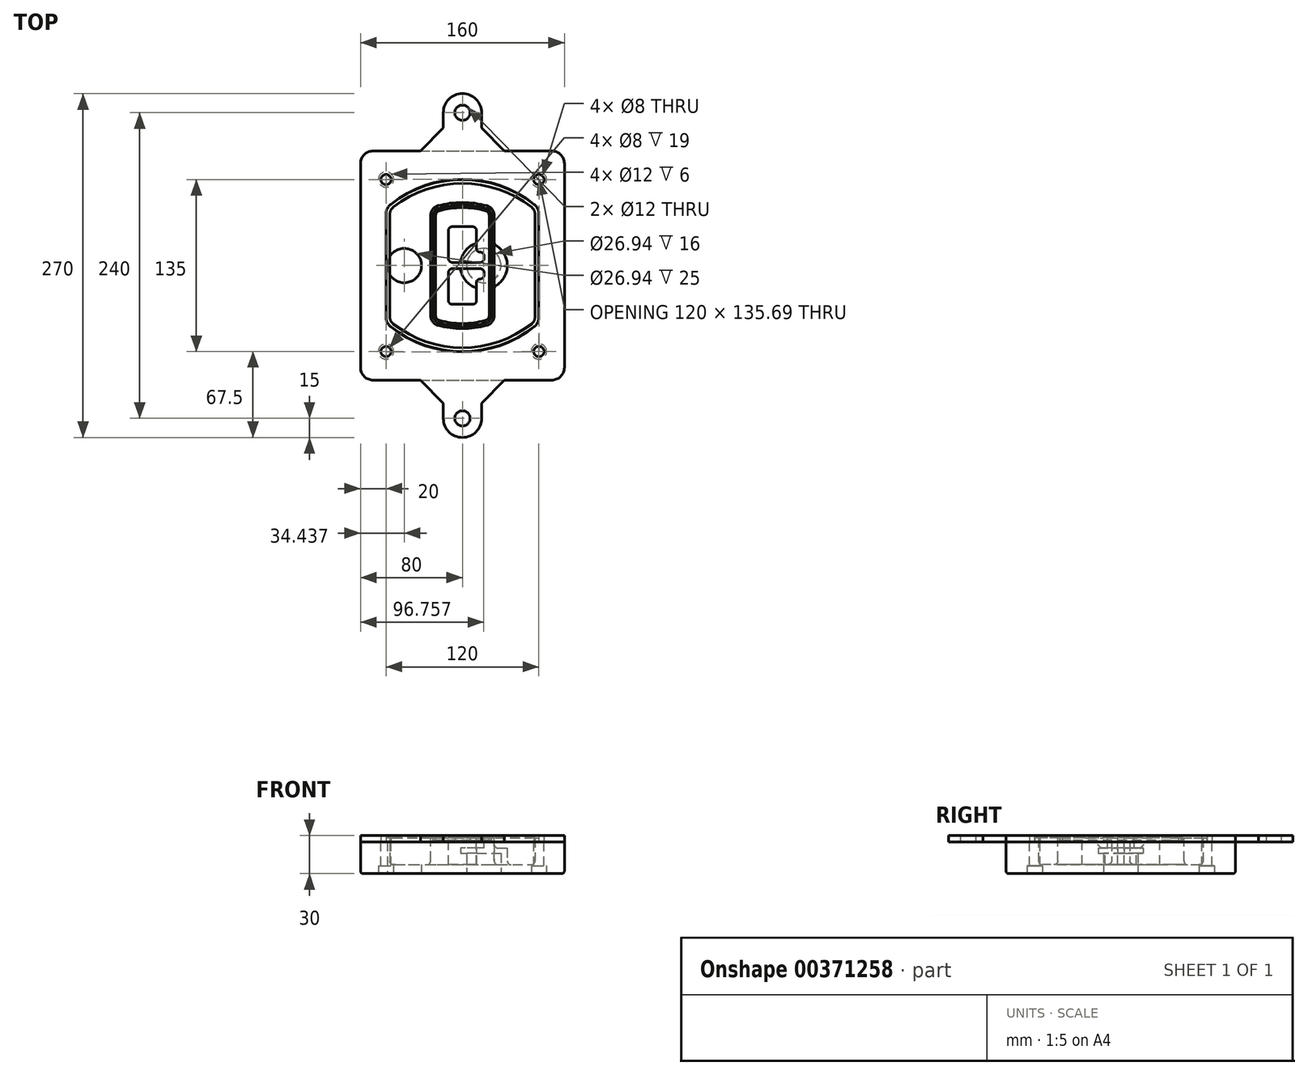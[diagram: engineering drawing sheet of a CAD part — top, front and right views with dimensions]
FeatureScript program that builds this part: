
annotation { "Feature Type Name" : "Feature", "Feature Type Description" : "" }
export const myFeature = defineFeature(function(context is Context, id is Id, definition is map)
    precondition{}
    {
        {
            var Q0;
            Q0=qCreatedBy(makeId("Top.planeOp"),FACE);
            var sketch = newSketch(context, id + "F0", { "sketchPlane" : qUnion([Q0])});
            skPoint(sketch, "E0.rect.middle", {"position": v(0, 0) * mm});
            skLineSegment(sketch, "E1.bottom", {"start": v(-70, -90) * mm, "end": v(70, -90) * mm});
            skLineSegment(sketch, "E1.top", {"start": v(-70, 90) * mm, "end": v(70, 90) * mm});
            skLineSegment(sketch, "E1.left", {"start": v(-80, -80) * mm, "end": v(-80, 80) * mm});
            skLineSegment(sketch, "E1.right", {"start": v(80, -80) * mm, "end": v(80, 80) * mm});
            skLineSegment(sketch, "E2", {"start": v(-80, 90) * mm, "end": v(80, -90) * mm, "construction": true});
            skLineSegment(sketch, "E3", {"start": v(80, 90) * mm, "end": v(-80, -90) * mm, "construction": true});
            skCircle(sketch, "E4", {"center": v(-60, 67.5) * mm, "radius": 4 * mm});
            skCircle(sketch, "E5", {"center": v(60, 67.5) * mm, "radius": 4 * mm});
            skCircle(sketch, "E6", {"center": v(60, -67.5) * mm, "radius": 4 * mm});
            skCircle(sketch, "E7", {"center": v(-60, -67.5) * mm, "radius": 4 * mm});
            skLineSegment(sketch, "E8", {"start": v(-60, 67.5) * mm, "end": v(60, 67.5) * mm, "construction": true});
            skLineSegment(sketch, "E9", {"start": v(60, 67.5) * mm, "end": v(60, -67.5) * mm, "construction": true});
            skLineSegment(sketch, "E10", {"start": v(60, -67.5) * mm, "end": v(-60, -67.5) * mm, "construction": true});
            skLineSegment(sketch, "E11", {"start": v(-60, -67.5) * mm, "end": v(-60, 67.5) * mm, "construction": true});
            skLineSegment(sketch, "E12", {"start": v(-60, 40.3) * mm, "end": v(-60, -40.3) * mm});
            skLineSegment(sketch, "E13", {"start": v(60, 40.3) * mm, "end": v(60, -40.3) * mm});
            skArc(sketch, "E14", {"start": v(56.15, 48.18) * mm, "mid": v(0, 67.5) * mm, "end": v(-56.15, 48.18) * mm});
            skArc(sketch, "E15", {"start": v(-56.15, -48.18) * mm, "mid": v(0, -67.5) * mm, "end": v(56.15, -48.18) * mm});
            skLineSegment(sketch, "E16", {"start": v(-60, 0) * mm, "end": v(60, 0) * mm, "construction": true});
            skPoint(sketch, "E17.visualSharp", {"position": v(-60, -45) * mm});
            skArc(sketch, "E17.filletArc", {"start": v(-60, -40.3) * mm, "mid": v(-58.99, -44.68) * mm, "end": v(-56.15, -48.18) * mm});
            skPoint(sketch, "E18.visualSharp", {"position": v(-60, 45) * mm});
            skArc(sketch, "E18.filletArc", {"start": v(-56.15, 48.18) * mm, "mid": v(-58.99, 44.68) * mm, "end": v(-60, 40.3) * mm});
            skPoint(sketch, "E19.visualSharp", {"position": v(60, 45) * mm});
            skArc(sketch, "E19.filletArc", {"start": v(60, 40.3) * mm, "mid": v(58.99, 44.68) * mm, "end": v(56.15, 48.18) * mm});
            skPoint(sketch, "E20.visualSharp", {"position": v(60, -45) * mm});
            skArc(sketch, "E20.filletArc", {"start": v(56.15, -48.18) * mm, "mid": v(58.99, -44.68) * mm, "end": v(60, -40.3) * mm});
            skPoint(sketch, "E21.visualSharp", {"position": v(-80, 90) * mm});
            skArc(sketch, "E21.filletArc", {"start": v(-70, 90) * mm, "mid": v(-77.07, 87.07) * mm, "end": v(-80, 80) * mm});
            skPoint(sketch, "E22.visualSharp", {"position": v(80, 90) * mm});
            skArc(sketch, "E22.filletArc", {"start": v(80, 80) * mm, "mid": v(77.07, 87.07) * mm, "end": v(70, 90) * mm});
            skPoint(sketch, "E23.visualSharp", {"position": v(80, -90) * mm});
            skArc(sketch, "E23.filletArc", {"start": v(70, -90) * mm, "mid": v(77.07, -87.07) * mm, "end": v(80, -80) * mm});
            skPoint(sketch, "E24.visualSharp", {"position": v(-80, -90) * mm});
            skArc(sketch, "E24.filletArc", {"start": v(-80, -80) * mm, "mid": v(-77.07, -87.07) * mm, "end": v(-70, -90) * mm});
            skArc(sketch, "E25.0", {"start": v(57, 40.3) * mm, "mid": v(56.3, 43.36) * mm, "end": v(54.3, 45.81) * mm});
            skLineSegment(sketch, "E25.1", {"start": v(57, 40.3) * mm, "end": v(57, -40.3) * mm});
            skArc(sketch, "E25.2", {"start": v(54.3, -45.81) * mm, "mid": v(56.3, -43.36) * mm, "end": v(57, -40.3) * mm});
            skArc(sketch, "E25.3", {"start": v(-54.3, -45.81) * mm, "mid": v(0, -64.5) * mm, "end": v(54.3, -45.81) * mm});
            skArc(sketch, "E25.4", {"start": v(-57, -40.3) * mm, "mid": v(-56.3, -43.36) * mm, "end": v(-54.3, -45.81) * mm});
            skArc(sketch, "E25.5", {"start": v(54.3, 45.81) * mm, "mid": v(0, 64.5) * mm, "end": v(-54.3, 45.81) * mm});
            skLineSegment(sketch, "E25.6", {"start": v(-57, 40.3) * mm, "end": v(-57, -40.3) * mm});
            skArc(sketch, "E25.7", {"start": v(-54.3, 45.81) * mm, "mid": v(-56.3, 43.36) * mm, "end": v(-57, 40.3) * mm});
            skArc(sketch, "E26.0", {"start": v(-58.62, 51.33) * mm, "mid": v(-62.58, 46.43) * mm, "end": v(-64, 40.3) * mm});
            skArc(sketch, "E26.1", {"start": v(58.62, 51.33) * mm, "mid": v(0, 71.5) * mm, "end": v(-58.62, 51.33) * mm});
            skArc(sketch, "E26.2", {"start": v(64, 40.3) * mm, "mid": v(62.58, 46.43) * mm, "end": v(58.62, 51.33) * mm});
            skLineSegment(sketch, "E26.3", {"start": v(64, 40.3) * mm, "end": v(64, -40.3) * mm});
            skArc(sketch, "E26.4", {"start": v(58.62, -51.33) * mm, "mid": v(62.58, -46.43) * mm, "end": v(64, -40.3) * mm});
            skLineSegment(sketch, "E26.5", {"start": v(-64, 40.3) * mm, "end": v(-64, -40.3) * mm});
            skArc(sketch, "E26.6", {"start": v(-58.62, -51.33) * mm, "mid": v(0, -71.5) * mm, "end": v(58.62, -51.33) * mm});
            skArc(sketch, "E26.7", {"start": v(-64, -40.3) * mm, "mid": v(-62.58, -46.43) * mm, "end": v(-58.62, -51.33) * mm});
            skSolve(sketch);
        }
        {
            var Q0;
            Q0=makeQuery(id+"F0.imprint","IMPRINT",FACE,{"disambiguationData":[TD([[makeQuery(id+"F0.imprint","IMPRINT",EDGE,{"derivedFrom":sQuery(id+"F0.wireOp",EDGE,"E1.bottom")}),1.0]])]});
            var Q1;
            Q1=makeQuery(id+"F0.imprint","IMPRINT",FACE,{"disambiguationData":[TD([[makeQuery(id+"F0.imprint","IMPRINT",EDGE,{"derivedFrom":sQuery(id+"F0.wireOp",EDGE,"E12")}),1.0]])]});
            var Q2;
            Q2=makeQuery(id+"F0.imprint","IMPRINT",FACE,{"disambiguationData":[TD([[makeQuery(id+"F0.imprint","IMPRINT",EDGE,{"derivedFrom":sQuery(id+"F0.wireOp",EDGE,"E25.0")}),1.0]])]});
            var Q3;
            Q3=makeQuery(id+"F0.imprint","IMPRINT",FACE,{"disambiguationData":[TD([[makeQuery(id+"F0.imprint","IMPRINT",EDGE,{"derivedFrom":sQuery(id+"F0.wireOp",EDGE,"E12")}),-1.0]])]});
            extrude(context, id + "F1", {"entities" : qUnion([Q0, Q1, Q2, Q3]), "oppositeDirection" : true, "depth" : 25 * mm});
        }
        {
            var Q0;
            Q0=makeQuery(id+"F0.imprint","IMPRINT",FACE,{"disambiguationData":[TD([[makeQuery(id+"F0.imprint","IMPRINT",EDGE,{"derivedFrom":sQuery(id+"F0.wireOp",EDGE,"E12")}),1.0]])]});
            extrude(context, id + "F2", {"entities" : qUnion([Q0]), "operationType" : NewBodyOperationType.ADD, "depth" : 3 * mm});
        }
        {
            var Q0;
            Q0=makeQuery(id+"F0.imprint","IMPRINT",FACE,{"disambiguationData":[TD([[makeQuery(id+"F0.imprint","IMPRINT",EDGE,{"derivedFrom":sQuery(id+"F0.wireOp",EDGE,"E25.0")}),1.0]])]});
            extrude(context, id + "F3", {"entities" : qUnion([Q0]), "operationType" : NewBodyOperationType.REMOVE, "oppositeDirection" : true, "depth" : 18 * mm});
        }
        {
            var Q0;
            Q0=makeQuery(id+"F2.opExtrude","CAP_FACE",FACE,{"disambiguationData":[OSD([sQuery(id+"F0.wireOp",EDGE,"E12"),sQuery(id+"F0.wireOp",EDGE,"E13"),sQuery(id+"F0.wireOp",EDGE,"E14"),sQuery(id+"F0.wireOp",EDGE,"E15"),sQuery(id+"F0.wireOp",EDGE,"E17.filletArc"),sQuery(id+"F0.wireOp",EDGE,"E18.filletArc"),sQuery(id+"F0.wireOp",EDGE,"E19.filletArc"),sQuery(id+"F0.wireOp",EDGE,"E20.filletArc"),sQuery(id+"F0.wireOp",EDGE,"E25.0"),sQuery(id+"F0.wireOp",EDGE,"E25.1"),sQuery(id+"F0.wireOp",EDGE,"E25.2"),sQuery(id+"F0.wireOp",EDGE,"E25.3"),sQuery(id+"F0.wireOp",EDGE,"E25.4"),sQuery(id+"F0.wireOp",EDGE,"E25.5"),sQuery(id+"F0.wireOp",EDGE,"E25.6"),sQuery(id+"F0.wireOp",EDGE,"E25.7")])],"isStart":false});
            var sketch = newSketch(context, id + "F4", { "sketchPlane" : qUnion([Q0])});
            skArc(sketch, "E27.0", {"start": v(-19.08, -46.97) * mm, "mid": v(0, -49.5) * mm, "end": v(19.08, -46.97) * mm});
            skArc(sketch, "E28.0", {"start": v(19.08, 46.97) * mm, "mid": v(0, 49.5) * mm, "end": v(-19.08, 46.97) * mm});
            skLineSegment(sketch, "E29", {"start": v(-25, 39.25) * mm, "end": v(-25, -39.25) * mm});
            skLineSegment(sketch, "E30", {"start": v(25, 39.25) * mm, "end": v(25, -39.25) * mm});
            skLineSegment(sketch, "E31", {"start": v(-25, 45.1) * mm, "end": v(25, 45.1) * mm, "construction": true});
            skLineSegment(sketch, "E32", {"start": v(-25, -45.1) * mm, "end": v(25, -45.1) * mm, "construction": true});
            skPoint(sketch, "E33.visualSharp", {"position": v(-25, 45.1) * mm});
            skArc(sketch, "E33.filletArc", {"start": v(-19.08, 46.97) * mm, "mid": v(-23.35, 44.11) * mm, "end": v(-25, 39.25) * mm});
            skPoint(sketch, "E34.visualSharp", {"position": v(25, 45.1) * mm});
            skArc(sketch, "E34.filletArc", {"start": v(25, 39.25) * mm, "mid": v(23.35, 44.11) * mm, "end": v(19.08, 46.97) * mm});
            skPoint(sketch, "E35.visualSharp", {"position": v(25, -45.1) * mm});
            skArc(sketch, "E35.filletArc", {"start": v(19.08, -46.97) * mm, "mid": v(23.35, -44.11) * mm, "end": v(25, -39.25) * mm});
            skPoint(sketch, "E36.visualSharp", {"position": v(-25, -45.1) * mm});
            skArc(sketch, "E36.filletArc", {"start": v(-25, -39.25) * mm, "mid": v(-23.35, -44.11) * mm, "end": v(-19.08, -46.97) * mm});
            skArc(sketch, "E37.0", {"start": v(54.3, 45.81) * mm, "mid": v(0, 64.5) * mm, "end": v(-54.3, 45.81) * mm});
            skArc(sketch, "E37.1", {"start": v(-54.3, 45.81) * mm, "mid": v(-56.3, 43.36) * mm, "end": v(-57, 40.3) * mm});
            skLineSegment(sketch, "E37.2", {"start": v(-57, 40.3) * mm, "end": v(-57, -40.3) * mm});
            skArc(sketch, "E37.3", {"start": v(-57, -40.3) * mm, "mid": v(-56.3, -43.36) * mm, "end": v(-54.3, -45.81) * mm});
            skArc(sketch, "E37.4", {"start": v(-54.3, -45.81) * mm, "mid": v(0, -64.5) * mm, "end": v(54.3, -45.81) * mm});
            skArc(sketch, "E37.5", {"start": v(54.3, -45.81) * mm, "mid": v(56.3, -43.36) * mm, "end": v(57, -40.3) * mm});
            skLineSegment(sketch, "E37.6", {"start": v(57, 40.3) * mm, "end": v(57, -40.3) * mm});
            skArc(sketch, "E37.7", {"start": v(57, 40.3) * mm, "mid": v(56.3, 43.36) * mm, "end": v(54.3, 45.81) * mm});
            skLineSegment(sketch, "E38.0", {"start": v(23, 39.25) * mm, "end": v(23, -39.25) * mm});
            skArc(sketch, "E38.1", {"start": v(18.56, -45.04) * mm, "mid": v(21.76, -42.9) * mm, "end": v(23, -39.25) * mm});
            skArc(sketch, "E38.2", {"start": v(-18.56, -45.04) * mm, "mid": v(0, -47.5) * mm, "end": v(18.56, -45.04) * mm});
            skArc(sketch, "E38.3", {"start": v(-23, -39.25) * mm, "mid": v(-21.76, -42.9) * mm, "end": v(-18.56, -45.04) * mm});
            skLineSegment(sketch, "E38.4", {"start": v(-23, 39.25) * mm, "end": v(-23, -39.25) * mm});
            skArc(sketch, "E38.5", {"start": v(23, 39.25) * mm, "mid": v(21.76, 42.9) * mm, "end": v(18.56, 45.04) * mm});
            skArc(sketch, "E38.6", {"start": v(-18.56, 45.04) * mm, "mid": v(-21.76, 42.9) * mm, "end": v(-23, 39.25) * mm});
            skArc(sketch, "E38.7", {"start": v(18.56, 45.04) * mm, "mid": v(0, 47.5) * mm, "end": v(-18.56, 45.04) * mm});
            skArc(sketch, "E39.0", {"start": v(21, 39.25) * mm, "mid": v(20.18, 41.68) * mm, "end": v(18.04, 43.1) * mm});
            skLineSegment(sketch, "E39.1", {"start": v(21, 39.25) * mm, "end": v(21, -39.25) * mm});
            skArc(sketch, "E39.2", {"start": v(18.04, -43.1) * mm, "mid": v(20.18, -41.68) * mm, "end": v(21, -39.25) * mm});
            skArc(sketch, "E39.3", {"start": v(-18.04, -43.1) * mm, "mid": v(0, -45.5) * mm, "end": v(18.04, -43.1) * mm});
            skArc(sketch, "E39.4", {"start": v(-21, -39.25) * mm, "mid": v(-20.18, -41.68) * mm, "end": v(-18.04, -43.1) * mm});
            skArc(sketch, "E39.5", {"start": v(18.04, 43.1) * mm, "mid": v(0, 45.5) * mm, "end": v(-18.04, 43.1) * mm});
            skLineSegment(sketch, "E39.6", {"start": v(-21, 39.25) * mm, "end": v(-21, -39.25) * mm});
            skArc(sketch, "E39.7", {"start": v(-18.04, 43.1) * mm, "mid": v(-20.18, 41.68) * mm, "end": v(-21, 39.25) * mm});
            skLineSegment(sketch, "E40", {"start": v(-25, 0) * mm, "end": v(25, 0) * mm, "construction": true});
            skLineSegment(sketch, "E41", {"start": v(-11, 5.5) * mm, "end": v(-11, 27.5) * mm});
            skLineSegment(sketch, "E42", {"start": v(-8, 30.5) * mm, "end": v(8, 30.5) * mm});
            skLineSegment(sketch, "E43", {"start": v(11, 27.5) * mm, "end": v(11, 13.5) * mm});
            skLineSegment(sketch, "E44", {"start": v(14, 10.5) * mm, "end": v(14, 10.5) * mm});
            skLineSegment(sketch, "E45", {"start": v(17, 7.5) * mm, "end": v(17, 5.5) * mm});
            skLineSegment(sketch, "E46", {"start": v(14, 2.5) * mm, "end": v(-8, 2.5) * mm});
            skPoint(sketch, "E47.visualSharp", {"position": v(-11, 30.5) * mm});
            skArc(sketch, "E47.filletArc", {"start": v(-8, 30.5) * mm, "mid": v(-10.12, 29.62) * mm, "end": v(-11, 27.5) * mm});
            skPoint(sketch, "E48.visualSharp", {"position": v(11, 30.5) * mm});
            skArc(sketch, "E48.filletArc", {"start": v(11, 27.5) * mm, "mid": v(10.12, 29.62) * mm, "end": v(8, 30.5) * mm});
            skPoint(sketch, "E49.visualSharp", {"position": v(11, 10.5) * mm});
            skArc(sketch, "E49.filletArc", {"start": v(11, 13.5) * mm, "mid": v(11.88, 11.38) * mm, "end": v(14, 10.5) * mm});
            skPoint(sketch, "E50.visualSharp", {"position": v(17, 10.5) * mm});
            skArc(sketch, "E50.filletArc", {"start": v(17, 7.5) * mm, "mid": v(16.12, 9.62) * mm, "end": v(14, 10.5) * mm});
            skPoint(sketch, "E51.visualSharp", {"position": v(17, 2.5) * mm});
            skArc(sketch, "E51.filletArc", {"start": v(14, 2.5) * mm, "mid": v(16.12, 3.38) * mm, "end": v(17, 5.5) * mm});
            skPoint(sketch, "E52.visualSharp", {"position": v(-11, 2.5) * mm});
            skArc(sketch, "E52.filletArc", {"start": v(-11, 5.5) * mm, "mid": v(-10.12, 3.38) * mm, "end": v(-8, 2.5) * mm});
            skLineSegment(sketch, "E53.0.MirrorCS", {"start": v(14, -2.5) * mm, "end": v(-8, -2.5) * mm});
            skArc(sketch, "E54.0.MirrorCS", {"start": v(-11, -5.5) * mm, "mid": v(-10.12, -3.38) * mm, "end": v(-8, -2.5) * mm});
            skLineSegment(sketch, "E55.0.MirrorCS", {"start": v(-11, -5.5) * mm, "end": v(-11, -27.5) * mm});
            skArc(sketch, "E56.0.MirrorCS", {"start": v(-8, -30.5) * mm, "mid": v(-10.12, -29.62) * mm, "end": v(-11, -27.5) * mm});
            skLineSegment(sketch, "E57.0.MirrorCS", {"start": v(-8, -30.5) * mm, "end": v(8, -30.5) * mm});
            skArc(sketch, "E58.0.MirrorCS", {"start": v(11, -27.5) * mm, "mid": v(10.12, -29.62) * mm, "end": v(8, -30.5) * mm});
            skLineSegment(sketch, "E59.0.MirrorCS", {"start": v(11, -27.5) * mm, "end": v(11, -13.5) * mm});
            skArc(sketch, "E60.0.MirrorCS", {"start": v(11, -13.5) * mm, "mid": v(11.88, -11.38) * mm, "end": v(14, -10.5) * mm});
            skArc(sketch, "E61.0.MirrorCS", {"start": v(17, -7.5) * mm, "mid": v(16.12, -9.62) * mm, "end": v(14, -10.5) * mm});
            skLineSegment(sketch, "E62.0.MirrorCS", {"start": v(17, -7.5) * mm, "end": v(17, -5.5) * mm});
            skArc(sketch, "E63.0.MirrorCS", {"start": v(14, -2.5) * mm, "mid": v(16.12, -3.38) * mm, "end": v(17, -5.5) * mm});
            skSolve(sketch);
        }
        {
            var Q0;
            Q0=makeQuery(id+"F4.imprint","IMPRINT",FACE,{"disambiguationData":[TD([[makeQuery(id+"F4.imprint","IMPRINT",EDGE,{"derivedFrom":sQuery(id+"F4.wireOp",EDGE,"E27.0")}),1.0]])]});
            var Q1;
            Q1=makeQuery(id+"F4.imprint","IMPRINT",FACE,{"disambiguationData":[TD([[makeQuery(id+"F4.imprint","IMPRINT",EDGE,{"derivedFrom":sQuery(id+"F4.wireOp",EDGE,"E38.0")}),-1.0]])]});
            var Q2;
            Q2=makeQuery(id+"F4.imprint","IMPRINT",FACE,{"disambiguationData":[TD([[makeQuery(id+"F4.imprint","IMPRINT",EDGE,{"derivedFrom":sQuery(id+"F4.wireOp",EDGE,"E39.0")}),1.0]])]});
            extrude(context, id + "F5", {"entities" : qUnion([Q0, Q1, Q2]), "operationType" : NewBodyOperationType.ADD, "endBound" : BoundingType.UP_TO_NEXT, "oppositeDirection" : true, "depth" : 25 * mm});
        }
        {
            var Q0;
            Q0=makeQuery(id+"F4.imprint","IMPRINT",FACE,{"disambiguationData":[TD([[makeQuery(id+"F4.imprint","IMPRINT",EDGE,{"derivedFrom":sQuery(id+"F4.wireOp",EDGE,"E38.0")}),-1.0]])]});
            extrude(context, id + "F6", {"entities" : qUnion([Q0]), "operationType" : NewBodyOperationType.REMOVE, "oppositeDirection" : true, "depth" : 2 * mm});
        }
        {
            var Q0;
            Q0=makeQuery(id+"F1.opExtrude","CAP_FACE",FACE,{"disambiguationData":[OSD([sQuery(id+"F0.wireOp",EDGE,"E1.bottom"),sQuery(id+"F0.wireOp",EDGE,"E1.top"),sQuery(id+"F0.wireOp",EDGE,"E1.left"),sQuery(id+"F0.wireOp",EDGE,"E1.right"),sQuery(id+"F0.wireOp",EDGE,"E4"),sQuery(id+"F0.wireOp",EDGE,"E5"),sQuery(id+"F0.wireOp",EDGE,"E6"),sQuery(id+"F0.wireOp",EDGE,"E7"),sQuery(id+"F0.wireOp",EDGE,"E21.filletArc"),sQuery(id+"F0.wireOp",EDGE,"E22.filletArc"),sQuery(id+"F0.wireOp",EDGE,"E23.filletArc"),sQuery(id+"F0.wireOp",EDGE,"E24.filletArc")])],"isStart":false});
            var sketch = newSketch(context, id + "F7", { "sketchPlane" : qUnion([Q0])});
            skCircle(sketch, "E64", {"center": v(16.76, 0) * mm, "radius": 13.47 * mm});
            skCircle(sketch, "E65", {"center": v(-45.56, 0) * mm, "radius": 13.47 * mm});
            skLineSegment(sketch, "E66", {"start": v(80, 0) * mm, "end": v(-80, 0) * mm});
            skCircle(sketch, "E67", {"center": v(16.76, 0) * mm, "radius": 18.47 * mm});
            skCircle(sketch, "E68", {"center": v(60, -67.5) * mm, "radius": 6 * mm});
            skCircle(sketch, "E69", {"center": v(-60, -67.5) * mm, "radius": 6 * mm});
            skCircle(sketch, "E70", {"center": v(-60, 67.5) * mm, "radius": 6 * mm});
            skCircle(sketch, "E71", {"center": v(60, 67.5) * mm, "radius": 6 * mm});
            skSolve(sketch);
        }
        {
            var Q0;
            {var subQ1=sQuery(id+"F7.wireOp",EDGE,"E66");var subQ4=sQuery(id+"F7.wireOp",EDGE,"E64");var subQ6=makeQuery(id+"F7.imprint","INTERSECT",VERTEX,{"disambiguationData":[OD(0.0)],"derivedFrom":[subQ4,subQ1]});Q0=makeQuery(id+"F7.imprint","IMPRINT",FACE,{"disambiguationData":[TD([[makeQuery(id+"F7.imprint","IMPRINT",EDGE,{"disambiguationData":[TD([[subQ6,-1.0]])],"derivedFrom":subQ4}),-1.0]])]});}
            var Q1;
            {var subQ0=sQuery(id+"F7.wireOp",EDGE,"E66");var subQ1=sQuery(id+"F7.wireOp",EDGE,"E64");var subQ3=makeQuery(id+"F7.imprint","INTERSECT",VERTEX,{"disambiguationData":[OD(0.0)],"derivedFrom":[subQ1,subQ0]});Q1=makeQuery(id+"F7.imprint","IMPRINT",FACE,{"disambiguationData":[TD([[makeQuery(id+"F7.imprint","IMPRINT",EDGE,{"disambiguationData":[TD([[subQ3,-1.0]])],"derivedFrom":subQ1}),1.0]])]});}
            var Q2;
            {var subQ0=sQuery(id+"F7.wireOp",EDGE,"E66");var subQ1=sQuery(id+"F7.wireOp",EDGE,"E64");var subQ3=makeQuery(id+"F7.imprint","INTERSECT",VERTEX,{"disambiguationData":[OD(0.0)],"derivedFrom":[subQ1,subQ0]});Q2=makeQuery(id+"F7.imprint","IMPRINT",FACE,{"disambiguationData":[TD([[makeQuery(id+"F7.imprint","IMPRINT",EDGE,{"disambiguationData":[TD([[subQ3,1.0]])],"derivedFrom":subQ1}),1.0]])]});}
            var Q3;
            {var subQ1=sQuery(id+"F7.wireOp",EDGE,"E66");var subQ4=sQuery(id+"F7.wireOp",EDGE,"E64");var subQ6=makeQuery(id+"F7.imprint","INTERSECT",VERTEX,{"disambiguationData":[OD(0.0)],"derivedFrom":[subQ4,subQ1]});Q3=makeQuery(id+"F7.imprint","IMPRINT",FACE,{"disambiguationData":[TD([[makeQuery(id+"F7.imprint","IMPRINT",EDGE,{"disambiguationData":[TD([[subQ6,1.0]])],"derivedFrom":subQ4}),-1.0]])]});}
            extrude(context, id + "F8", {"entities" : qUnion([Q0, Q1, Q2, Q3]), "operationType" : NewBodyOperationType.ADD, "oppositeDirection" : true, "depth" : 20 * mm});
        }
        {
            var Q0;
            {var subQ0=sQuery(id+"F7.wireOp",EDGE,"E66");var subQ1=sQuery(id+"F7.wireOp",EDGE,"E64");var subQ3=makeQuery(id+"F7.imprint","INTERSECT",VERTEX,{"disambiguationData":[OD(0.0)],"derivedFrom":[subQ1,subQ0]});Q0=makeQuery(id+"F7.imprint","IMPRINT",FACE,{"disambiguationData":[TD([[makeQuery(id+"F7.imprint","IMPRINT",EDGE,{"disambiguationData":[TD([[subQ3,-1.0]])],"derivedFrom":subQ1}),1.0]])]});}
            var Q1;
            {var subQ0=sQuery(id+"F7.wireOp",EDGE,"E66");var subQ1=sQuery(id+"F7.wireOp",EDGE,"E64");var subQ3=makeQuery(id+"F7.imprint","INTERSECT",VERTEX,{"disambiguationData":[OD(0.0)],"derivedFrom":[subQ1,subQ0]});Q1=makeQuery(id+"F7.imprint","IMPRINT",FACE,{"disambiguationData":[TD([[makeQuery(id+"F7.imprint","IMPRINT",EDGE,{"disambiguationData":[TD([[subQ3,1.0]])],"derivedFrom":subQ1}),1.0]])]});}
            extrude(context, id + "F9", {"entities" : qUnion([Q0, Q1]), "operationType" : NewBodyOperationType.REMOVE, "oppositeDirection" : true, "depth" : 16 * mm});
        }
        {
            var Q0;
            {var subQ0=sQuery(id+"F7.wireOp",EDGE,"E66");var subQ1=sQuery(id+"F7.wireOp",EDGE,"E65");var subQ3=makeQuery(id+"F7.imprint","INTERSECT",VERTEX,{"disambiguationData":[OD(0.0)],"derivedFrom":[subQ1,subQ0]});Q0=makeQuery(id+"F7.imprint","IMPRINT",FACE,{"disambiguationData":[TD([[makeQuery(id+"F7.imprint","IMPRINT",EDGE,{"disambiguationData":[TD([[subQ3,-1.0]])],"derivedFrom":subQ1}),1.0]])]});}
            var Q1;
            {var subQ0=sQuery(id+"F7.wireOp",EDGE,"E66");var subQ1=sQuery(id+"F7.wireOp",EDGE,"E65");var subQ3=makeQuery(id+"F7.imprint","INTERSECT",VERTEX,{"disambiguationData":[OD(0.0)],"derivedFrom":[subQ1,subQ0]});Q1=makeQuery(id+"F7.imprint","IMPRINT",FACE,{"disambiguationData":[TD([[makeQuery(id+"F7.imprint","IMPRINT",EDGE,{"disambiguationData":[TD([[subQ3,1.0]])],"derivedFrom":subQ1}),1.0]])]});}
            extrude(context, id + "F10", {"entities" : qUnion([Q0, Q1]), "operationType" : NewBodyOperationType.REMOVE, "oppositeDirection" : true, "depth" : 25 * mm});
        }
        {
            var Q0;
            Q0=makeQuery(id+"F7.imprint","IMPRINT",FACE,{"disambiguationData":[TD([[makeQuery(id+"F7.imprint","IMPRINT",EDGE,{"derivedFrom":sQuery(id+"F7.wireOp",EDGE,"E68")}),1.0]])]});
            var Q1;
            Q1=makeQuery(id+"F7.imprint","IMPRINT",FACE,{"disambiguationData":[TD([[makeQuery(id+"F7.imprint","IMPRINT",EDGE,{"derivedFrom":makeQuery(id+"F1.opExtrude","CAP_EDGE",EDGE,{"disambiguationData":[OSD([sQuery(id+"F0.wireOp",EDGE,"E5")])],"isStart":false})}),-1.0]])]});
            var Q2;
            Q2=makeQuery(id+"F7.imprint","IMPRINT",FACE,{"disambiguationData":[TD([[makeQuery(id+"F7.imprint","IMPRINT",EDGE,{"derivedFrom":sQuery(id+"F7.wireOp",EDGE,"E69")}),1.0]])]});
            var Q3;
            Q3=makeQuery(id+"F7.imprint","IMPRINT",FACE,{"disambiguationData":[TD([[makeQuery(id+"F7.imprint","IMPRINT",EDGE,{"derivedFrom":makeQuery(id+"F1.opExtrude","CAP_EDGE",EDGE,{"disambiguationData":[OSD([sQuery(id+"F0.wireOp",EDGE,"E4")])],"isStart":false})}),-1.0]])]});
            var Q4;
            Q4=makeQuery(id+"F7.imprint","IMPRINT",FACE,{"disambiguationData":[TD([[makeQuery(id+"F7.imprint","IMPRINT",EDGE,{"derivedFrom":sQuery(id+"F7.wireOp",EDGE,"E70")}),1.0]])]});
            var Q5;
            Q5=makeQuery(id+"F7.imprint","IMPRINT",FACE,{"disambiguationData":[TD([[makeQuery(id+"F7.imprint","IMPRINT",EDGE,{"derivedFrom":makeQuery(id+"F1.opExtrude","CAP_EDGE",EDGE,{"disambiguationData":[OSD([sQuery(id+"F0.wireOp",EDGE,"E7")])],"isStart":false})}),-1.0]])]});
            var Q6;
            Q6=makeQuery(id+"F7.imprint","IMPRINT",FACE,{"disambiguationData":[TD([[makeQuery(id+"F7.imprint","IMPRINT",EDGE,{"derivedFrom":sQuery(id+"F7.wireOp",EDGE,"E71")}),1.0]])]});
            var Q7;
            Q7=makeQuery(id+"F7.imprint","IMPRINT",FACE,{"disambiguationData":[TD([[makeQuery(id+"F7.imprint","IMPRINT",EDGE,{"derivedFrom":makeQuery(id+"F1.opExtrude","CAP_EDGE",EDGE,{"disambiguationData":[OSD([sQuery(id+"F0.wireOp",EDGE,"E6")])],"isStart":false})}),-1.0]])]});
            extrude(context, id + "F11", {"entities" : qUnion([Q0, Q1, Q2, Q3, Q4, Q5, Q6, Q7]), "operationType" : NewBodyOperationType.REMOVE, "oppositeDirection" : true, "depth" : 6 * mm});
        }
        {
            var Q0;
            Q0=makeQuery(id+"F9.boolean.opBoolean","COPY",FACE,{"derivedFrom":makeQuery(id+"F9.opExtrude","CAP_FACE",FACE,{"disambiguationData":[OSD([sQuery(id+"F7.wireOp",EDGE,"E64")])],"isStart":false})});
            var sketch = newSketch(context, id + "F12", { "sketchPlane" : qUnion([Q0])});
            skArc(sketch, "E72.0", {"start": v(11, 17.55) * mm, "mid": v(2.57, 11.82) * mm, "end": v(-1.54, 2.5) * mm});
            skArc(sketch, "E72.1", {"start": v(-1.54, -2.5) * mm, "mid": v(2.57, -11.82) * mm, "end": v(11, -17.55) * mm});
            skLineSegment(sketch, "E73", {"start": v(-1.54, -2.5) * mm, "end": v(14, -2.5) * mm});
            skLineSegment(sketch, "E74.0", {"start": v(14, 2.5) * mm, "end": v(-1.54, 2.5) * mm});
            skArc(sketch, "E74.1", {"start": v(14, 2.5) * mm, "mid": v(16.12, 3.38) * mm, "end": v(17, 5.5) * mm});
            skLineSegment(sketch, "E74.2", {"start": v(17, 7.5) * mm, "end": v(17, 5.5) * mm});
            skArc(sketch, "E74.3", {"start": v(17, 7.5) * mm, "mid": v(16.12, 9.62) * mm, "end": v(14, 10.5) * mm});
            skArc(sketch, "E74.4", {"start": v(11, 13.5) * mm, "mid": v(11.88, 11.38) * mm, "end": v(14, 10.5) * mm});
            skLineSegment(sketch, "E74.5", {"start": v(11, 17.55) * mm, "end": v(11, 13.5) * mm});
            skLineSegment(sketch, "E74.7", {"start": v(14, -2.5) * mm, "end": v(-1.54, -2.5) * mm});
            skArc(sketch, "E74.8", {"start": v(14, -2.5) * mm, "mid": v(16.12, -3.38) * mm, "end": v(17, -5.5) * mm});
            skLineSegment(sketch, "E74.9", {"start": v(17, -7.5) * mm, "end": v(17, -5.5) * mm});
            skArc(sketch, "E74.10", {"start": v(17, -7.5) * mm, "mid": v(16.12, -9.62) * mm, "end": v(14, -10.5) * mm});
            skArc(sketch, "E74.11", {"start": v(11, -13.5) * mm, "mid": v(11.88, -11.38) * mm, "end": v(14, -10.5) * mm});
            skLineSegment(sketch, "E74.12", {"start": v(11, -17.55) * mm, "end": v(11, -13.5) * mm});
            skPoint(sketch, "E75.orphan", {"position": v(11, -27.5) * mm});
            skPoint(sketch, "E76.orphan", {"position": v(-8, -2.5) * mm});
            skPoint(sketch, "E77.orphan", {"position": v(-8, 2.5) * mm});
            skPoint(sketch, "E78.orphan", {"position": v(11, 27.5) * mm});
            skSolve(sketch);
        }
        {
            var Q0;
            {var subQ7=sQuery(id+"F12.wireOp",EDGE,"E72.0");var subQ14=sQuery(id+"F12.wireOp",EDGE,"E72.1");var subQ16=sQuery(id+"F12.wireOp",EDGE,"E74.1");var subQ18=sQuery(id+"F12.wireOp",EDGE,"E74.8");Q0=qUnion([makeQuery(id+"F12.imprint","IMPRINT",FACE,{"disambiguationData":[TD([[makeQuery(id+"F12.imprint","IMPRINT",EDGE,{"derivedFrom":subQ7}),1.0]])]}),makeQuery(id+"F12.imprint","IMPRINT",FACE,{"disambiguationData":[TD([[makeQuery(id+"F12.imprint","IMPRINT",EDGE,{"derivedFrom":subQ14}),1.0]])]}),makeQuery(id+"F12.imprint","IMPRINT",FACE,{"disambiguationData":[TD([[makeQuery(id+"F12.imprint","IMPRINT",EDGE,{"derivedFrom":subQ16}),1.0]])]}),makeQuery(id+"F12.imprint","IMPRINT",FACE,{"disambiguationData":[TD([[makeQuery(id+"F12.imprint","IMPRINT",EDGE,{"derivedFrom":subQ18}),-1.0]])]})]);}
            var Q1;
            Q1=makeQuery(id+"F5.boolean.opBoolean","SPLIT",FACE,{"disambiguationData":[TD([makeQuery(id+"F5.opExtrude","SWEPT_FACE",FACE,{"disambiguationData":[OSD([sQuery(id+"F4.wireOp",EDGE,"E41")])]})])],"derivedFrom":makeQuery(id+"F3.boolean.opBoolean","COPY",FACE,{"derivedFrom":makeQuery(id+"F3.opExtrude","CAP_FACE",FACE,{"disambiguationData":[OSD([sQuery(id+"F0.wireOp",EDGE,"E25.0"),sQuery(id+"F0.wireOp",EDGE,"E25.1"),sQuery(id+"F0.wireOp",EDGE,"E25.2"),sQuery(id+"F0.wireOp",EDGE,"E25.3"),sQuery(id+"F0.wireOp",EDGE,"E25.4"),sQuery(id+"F0.wireOp",EDGE,"E25.5"),sQuery(id+"F0.wireOp",EDGE,"E25.6"),sQuery(id+"F0.wireOp",EDGE,"E25.7")])],"isStart":false})})});
            extrude(context, id + "F13", {"entities" : qUnion([Q0]), "operationType" : NewBodyOperationType.REMOVE, "endBound" : BoundingType.UP_TO_SURFACE, "endBoundEntityFace" : qUnion([Q1]), "depth" : 25 * mm});
        }
        {
            var Q0;
            Q0=makeQuery(id+"F3.boolean.opBoolean","COPY",EDGE,{"derivedFrom":makeQuery(id+"F3.opExtrude","CAP_EDGE",EDGE,{"disambiguationData":[OSD([sQuery(id+"F0.wireOp",EDGE,"E25.6")])],"isStart":false})});
            var Q1;
            Q1=makeQuery(id+"F8.boolean.opBoolean","INTERSECT",EDGE,{"derivedFrom":[makeQuery(id+"F5.opExtrude","SWEPT_FACE",FACE,{"disambiguationData":[OSD([sQuery(id+"F4.wireOp",EDGE,"E30")])]}),makeQuery(id+"F8.opExtrude","CAP_FACE",FACE,{"disambiguationData":[OSD([sQuery(id+"F7.wireOp",EDGE,"E67")])],"isStart":false})]});
            var Q2;
            Q2=makeQuery(id+"F8.boolean.opBoolean","INTERSECT",EDGE,{"disambiguationData":[OD(1.0)],"derivedFrom":[makeQuery(id+"F5.opExtrude","SWEPT_FACE",FACE,{"disambiguationData":[OSD([sQuery(id+"F4.wireOp",EDGE,"E30")])]}),makeQuery(id+"F8.opExtrude","SWEPT_FACE",FACE,{"disambiguationData":[OSD([sQuery(id+"F7.wireOp",EDGE,"E67")])]})]});
            var Q3;
            {var subQ0=sQuery(id+"F4.wireOp",EDGE,"E30");Q3=makeQuery(id+"F8.boolean.opBoolean","SPLIT",EDGE,{"disambiguationData":[TD([makeQuery(id+"F5.opExtrude","SWEPT_FACE",FACE,{"disambiguationData":[OSD([sQuery(id+"F4.wireOp",EDGE,"E35.filletArc")])]})])],"derivedFrom":makeQuery(id+"F5.opExtrude","CAP_EDGE",EDGE,{"disambiguationData":[OSD([subQ0])],"isStart":false})});}
            var Q4;
            {var subQ0=sQuery(id+"F0.wireOp",EDGE,"E25.7");var subQ1=sQuery(id+"F0.wireOp",EDGE,"E25.1");var subQ2=sQuery(id+"F0.wireOp",EDGE,"E25.6");var subQ3=sQuery(id+"F0.wireOp",EDGE,"E25.5");var subQ4=sQuery(id+"F0.wireOp",EDGE,"E25.4");var subQ5=sQuery(id+"F0.wireOp",EDGE,"E25.0");var subQ6=sQuery(id+"F0.wireOp",EDGE,"E25.2");var subQ7=sQuery(id+"F0.wireOp",EDGE,"E25.3");Q4=makeQuery(id+"F8.boolean.opBoolean","INTERSECT",EDGE,{"derivedFrom":[makeQuery(id+"F5.boolean.opBoolean","SPLIT",FACE,{"disambiguationData":[TD([makeQuery(id+"F2.opExtrude","SWEPT_FACE",FACE,{"disambiguationData":[OSD([subQ5])]})])],"derivedFrom":makeQuery(id+"F3.boolean.opBoolean","COPY",FACE,{"derivedFrom":makeQuery(id+"F3.opExtrude","CAP_FACE",FACE,{"disambiguationData":[OSD([subQ5,subQ1,subQ6,subQ7,subQ4,subQ3,subQ2,subQ0])],"isStart":false})})}),makeQuery(id+"F8.opExtrude","SWEPT_FACE",FACE,{"disambiguationData":[OSD([sQuery(id+"F7.wireOp",EDGE,"E67")])]})]});}
            var Q5;
            Q5=makeQuery(id+"F8.boolean.opBoolean","INTERSECT",EDGE,{"disambiguationData":[OD(0.0)],"derivedFrom":[makeQuery(id+"F5.opExtrude","SWEPT_FACE",FACE,{"disambiguationData":[OSD([sQuery(id+"F4.wireOp",EDGE,"E30")])]}),makeQuery(id+"F8.opExtrude","SWEPT_FACE",FACE,{"disambiguationData":[OSD([sQuery(id+"F7.wireOp",EDGE,"E67")])]})]});
            fillet(context, id + "F14", {"entities" : qUnion([Q0, Q1, Q2, Q3, Q4, Q5]), "radius" : 3 * mm, "tangentPropagation" : true, "allowEdgeOverflow" : false});
        }
        {
            var Q0;
            Q0=makeQuery(id+"F1.opExtrude","CAP_EDGE",EDGE,{"disambiguationData":[OSD([sQuery(id+"F0.wireOp",EDGE,"E1.bottom")])],"isStart":false});
            fillet(context, id + "F15", {"entities" : qUnion([Q0]), "radius" : 2 * mm, "tangentPropagation" : true, "allowEdgeOverflow" : false});
        }
        {
            var Q0;
            {var subQ0=sQuery(id+"F0.wireOp",EDGE,"E21.filletArc");var subQ1=sQuery(id+"F0.wireOp",EDGE,"E7");var subQ2=sQuery(id+"F0.wireOp",EDGE,"E6");var subQ3=sQuery(id+"F0.wireOp",EDGE,"E5");var subQ4=sQuery(id+"F0.wireOp",EDGE,"E4");var subQ5=sQuery(id+"F0.wireOp",EDGE,"E22.filletArc");var subQ6=sQuery(id+"F0.wireOp",EDGE,"E1.bottom");var subQ7=sQuery(id+"F0.wireOp",EDGE,"E1.right");var subQ8=sQuery(id+"F0.wireOp",EDGE,"E1.top");var subQ9=sQuery(id+"F0.wireOp",EDGE,"E1.left");var subQ10=sQuery(id+"F0.wireOp",EDGE,"E23.filletArc");var subQ11=sQuery(id+"F0.wireOp",EDGE,"E24.filletArc");Q0=makeQuery(id+"F2.boolean.opBoolean","SPLIT",FACE,{"disambiguationData":[TD([makeQuery(id+"F1.opExtrude","SWEPT_FACE",FACE,{"disambiguationData":[OSD([subQ6])]})])],"derivedFrom":makeQuery(id+"F1.opExtrude","CAP_FACE",FACE,{"disambiguationData":[OSD([subQ6,subQ8,subQ9,subQ7,subQ4,subQ3,subQ2,subQ1,subQ0,subQ5,subQ10,subQ11])],"isStart":true})});}
            var sketch = newSketch(context, id + "F16", { "sketchPlane" : qUnion([Q0])});
            skLineSegment(sketch, "E79", {"start": v(0, 90) * mm, "end": v(0, 120) * mm, "construction": true});
            skCircle(sketch, "E80", {"center": v(0, 120) * mm, "radius": 6 * mm});
            skLineSegment(sketch, "E81", {"start": v(-15, 120) * mm, "end": v(-15, 108) * mm});
            skLineSegment(sketch, "E82", {"start": v(15, 120) * mm, "end": v(15, 108) * mm});
            skArc(sketch, "E83", {"start": v(15, 120) * mm, "mid": v(0, 135) * mm, "end": v(-15, 120) * mm});
            skLineSegment(sketch, "E84", {"start": v(-15, 108) * mm, "end": v(-33, 90) * mm});
            skLineSegment(sketch, "E85", {"start": v(15, 108) * mm, "end": v(33, 90) * mm});
            skPoint(sketch, "E86.startSnap0", {"position": v(-80, 0) * mm});
            skLineSegment(sketch, "E87.MirrorCS", {"start": v(15, -108) * mm, "end": v(33, -90) * mm});
            skLineSegment(sketch, "E88.MirrorCS", {"start": v(15, -120) * mm, "end": v(15, -108) * mm});
            skArc(sketch, "E89.MirrorCS", {"start": v(15, -120) * mm, "mid": v(0, -135) * mm, "end": v(-15, -120) * mm});
            skCircle(sketch, "E90.MirrorC", {"center": v(0, -120) * mm, "radius": 6 * mm});
            skLineSegment(sketch, "E91.MirrorCS", {"start": v(0, -90) * mm, "end": v(0, -120) * mm, "construction": true});
            skLineSegment(sketch, "E92.MirrorCS", {"start": v(-15, -120) * mm, "end": v(-15, -108) * mm});
            skLineSegment(sketch, "E93.MirrorCS", {"start": v(-15, -108) * mm, "end": v(-33, -90) * mm});
            skLineSegment(sketch, "E94", {"start": v(-70, 90) * mm, "end": v(-33, 90) * mm});
            skLineSegment(sketch, "E95", {"start": v(33, 90) * mm, "end": v(70, 90) * mm});
            skLineSegment(sketch, "E96", {"start": v(33, -90) * mm, "end": v(70, -90) * mm});
            skLineSegment(sketch, "E97", {"start": v(-33, -90) * mm, "end": v(-70, -90) * mm});
            skLineSegment(sketch, "E98", {"start": v(-80, 80) * mm, "end": v(-80, -80) * mm});
            skLineSegment(sketch, "E99", {"start": v(80, -80) * mm, "end": v(80, 80) * mm});
            skLineSegment(sketch, "E100", {"start": v(-60, -40.3) * mm, "end": v(-60, 40.3) * mm});
            skLineSegment(sketch, "E101", {"start": v(60, -40.3) * mm, "end": v(60, 40.3) * mm});
            skArc(sketch, "E102", {"start": v(-80, -80) * mm, "mid": v(-77.07, -87.07) * mm, "end": v(-70, -90) * mm});
            skArc(sketch, "E103", {"start": v(-70, 90) * mm, "mid": v(-77.07, 87.07) * mm, "end": v(-80, 80) * mm});
            skArc(sketch, "E104", {"start": v(80, 80) * mm, "mid": v(77.07, 87.07) * mm, "end": v(70, 90) * mm});
            skArc(sketch, "E105", {"start": v(70, -90) * mm, "mid": v(77.07, -87.07) * mm, "end": v(80, -80) * mm});
            skArc(sketch, "E106", {"start": v(-56.15, 48.18) * mm, "mid": v(-58.99, 44.68) * mm, "end": v(-60, 40.3) * mm});
            skArc(sketch, "E107", {"start": v(-60, -40.3) * mm, "mid": v(-58.99, -44.68) * mm, "end": v(-56.15, -48.18) * mm});
            skArc(sketch, "E108", {"start": v(60, 40.3) * mm, "mid": v(58.99, 44.68) * mm, "end": v(56.15, 48.18) * mm});
            skArc(sketch, "E109", {"start": v(56.15, -48.18) * mm, "mid": v(58.99, -44.68) * mm, "end": v(60, -40.3) * mm});
            skCircle(sketch, "E110", {"center": v(-60, -67.5) * mm, "radius": 4 * mm});
            skCircle(sketch, "E111", {"center": v(60, -67.5) * mm, "radius": 4 * mm});
            skCircle(sketch, "E112", {"center": v(60, 67.5) * mm, "radius": 4 * mm});
            skCircle(sketch, "E113", {"center": v(-60, 67.5) * mm, "radius": 4 * mm});
            skArc(sketch, "E114", {"start": v(56.15, 48.18) * mm, "mid": v(0, 67.84) * mm, "end": v(-56.15, 48.18) * mm});
            skArc(sketch, "E115", {"start": v(-56.15, -48.18) * mm, "mid": v(0, -67.84) * mm, "end": v(56.15, -48.18) * mm});
            skSolve(sketch);
        }
        {
            var Q0;
            Q0 = qSketchRegion(id + "F16", true);
            extrude(context, id + "F17", {"entities" : qUnion([Q0]), "depth" : 5 * mm});
        }
    });
